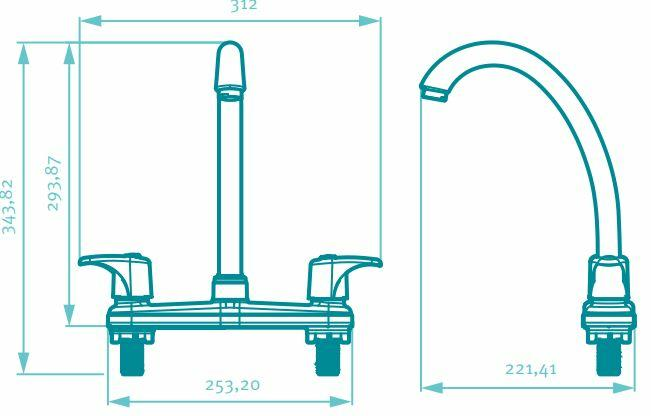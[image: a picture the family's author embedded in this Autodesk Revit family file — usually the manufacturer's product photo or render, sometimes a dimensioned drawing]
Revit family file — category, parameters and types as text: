
# Revit family: 435100001_Griferia Lavaplatos Dalia 8 Pulgadas
name_source: partatom
category: Plumbing Fixtures
units: mm (PartAtom-declared; Revit-internal decimal feet)

## family parameters
Cut with Voids When Loaded = No
Host = Face
OmniClass Number = 23.31.11.00
OmniClass Title = Faucets
Part Type = Normal
Room Calculation Point = No
Round Connector Dimension = Use Diameter
Shared = No

## types (1)
- 435100001_Griferia Lavaplatos Dalia 8 Pulgadas
    Alto = 344 mm
    Ancho = 312 mm  [stored 1.02362 ft]
    Capacidad de flujo = 6,3 L/min.
    Creado por = BIMBAU
    Default Elevation = 1219 mm
    Description = Resistente a la corrosión, pelado y decoloración por agua. Recubrimientos no tóxico. Condición de servicio recomendada, uso doméstico. Material Metálico (latón), mayor durabilidad, sistema apertura a 90º grados. Genera un chorro de agua espumoso, agradable al tacto y a la vista, ahorra agua. Acabado brillante, brinda la apariencia de material acero.nnGarantía por 45 añosn
    Fecha de creación = 06/04/2021
    Garantía = 30  Años Grival - 2 Años Cromado
    Manufacturer = Grival
    Material = Corona_Aluminio
    Model = Conjunto  Griferia Lavaplatos 8 pulgadas Dalia
    Peso Bruto aprox = 773,5 gr. / 1,7 lb.
    Peso Neto aprox = 471,5 gr. / 1,03 lb.
    Profundidad = 221 mm
    Referencia = 435100001
    Temperaturas máxima de trabajo = 5ºC a 71ºC.
    URL = https://www.grival.com
    Vida útil = 500.000 ciclos.

note: [stored X ft] marks values corroborated as IEEE doubles in the binary element streams (Revit-internal decimal feet)

## geometry (parser evidence)
native form markers: Sweep x3
no freeform markers — native parametric forms only
